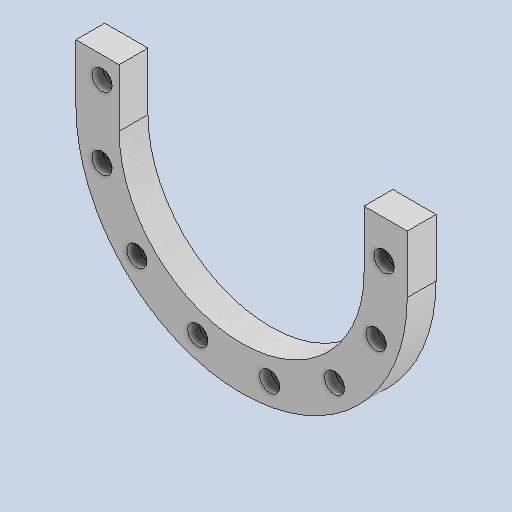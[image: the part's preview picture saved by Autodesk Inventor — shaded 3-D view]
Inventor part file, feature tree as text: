
AUTODESK INVENTOR PART (.ipt)
format: ipt  version: 2024.2 (Build 282272000, 272)  size: 171,008 bytes
history: native  units: mm
features: extrude x3, sketch x3, pattern_circular x1
ambient origin geometry x8: Origin, YZ Plane, XZ Plane, XY Plane, X Axis, Y Axis, Z Axis, Center Point
bodies: Solid1 (feature_tree)
feature tree (7):
  extrude  "Extrusion1"  Depth=400.0mm
  extrude  "Extrusion4"  TaperAngle=0.0deg  [1 undecoded]
  extrude  "Extrusion5"  Depth=15.0mm TaperAngle=0.0deg
  pattern_circular  "Circular Pattern3"  Count=8  [1 undecoded]
  sketch  "Sketch1"  dims[d2=40.0mm d3=0.0mm d13=400.0mm]
  sketch  "Sketch4"  dims[d17=18.0mm d18=0.0mm d19=0.0mm]
  sketch  "Sketch5"  dims[d23=28.0mm d24=15.0mm d25=0.0mm d26=80.0mm d27=200.0mm d35=1.963495mm d36=60.0mm d37=80.0mm d38=202.5deg]
note: 2 required parameter values undecoded (feature->parameter linkage not recoverable at this tier; creation-order binding heuristic only, values carry confidence <= 0.55)
